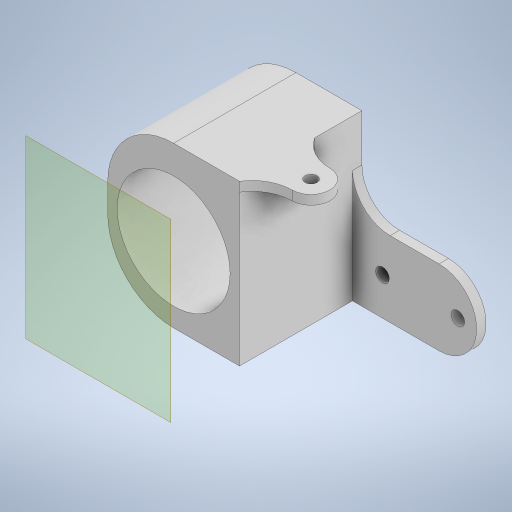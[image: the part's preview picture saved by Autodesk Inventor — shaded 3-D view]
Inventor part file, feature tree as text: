
AUTODESK INVENTOR PART (.ipt)
format: ipt  version: 2024 (Build 280153000, 153)  size: 759,808 bytes
history: native  units: in
note: dims shown in document units (in); Inventor stores cm internally (conversion verified against a paired STEP export)
features: extrude x5, sketch x5, projected_geometry x3, fillet x1, plane x1, mirror x1
ambient origin geometry x8: Origin, YZ Plane, XZ Plane, XY Plane, X Axis, Y Axis, Z Axis, Center Point
bodies: Solid1 (feature_tree)
feature tree (16):
  extrude  "Extrusion1"  Depth=2.0in
  extrude  "Extrusion2"  Depth=1.5in
  extrude  "Extrusion3"  Depth=0.09in
  extrude  "Extrusion4"  Depth=0.125in TaperAngle=0.0deg
  fillet  "Fillet2"  Radius=0.4in
  plane  "Work Plane1"
  mirror  "Mirror1"
  extrude  "Extrusion5"  Depth=0.125in
  sketch  "Sketch1"  dims[d1=1.5in d2=2.0in]
  sketch  "Sketch3"  dims[d3=1.5in d4=0.0in d6=1.05in]
  projected_geometry  "Projected Loop2"
  sketch  "Sketch4"  dims[d7=0.09in d8=0.61in]
  projected_geometry  "Projected Loop3"
  sketch  "Sketch6"  dims[d9=2.3622in d11=360.0deg d13=0.125in d14=0.0in d15=0.4in]
  projected_geometry  "Projected Loop5"
  sketch  "Sketch7"  dims[d16=1.0in d17=0.18in d18=1.0in d19=0.25in d20=0.125in d21=0.0in d22=1.75in d24=0.45in d25=0.16in d26=0.25in d27=0.25in d28=0.125in d29=0.0in d30=0.5in d32=0.125in d33=1.0in d34=0.0in d35=0.0in d36=1.0in d37=0.125in]
